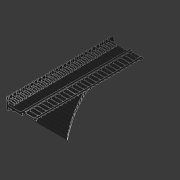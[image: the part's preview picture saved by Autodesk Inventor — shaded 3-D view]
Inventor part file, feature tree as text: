
AUTODESK INVENTOR PART (.ipt)
format: ipt  version: 2020.2 (Build 242310000, 310)  size: 4,468,224 bytes
history: native  units: in
note: dims shown in document units (in); Inventor stores cm internally (conversion verified against a paired STEP export)
features: other x35, extrude x15, loft x3, fillet x2, pattern_linear x2, sketch x1, projected_geometry x1
ambient origin geometry x8: Origin, YZ Plane, XZ Plane, XY Plane, X Axis, Y Axis, Z Axis, Center Point
bodies: Body1 (feature_tree), Body2 (feature_tree)
feature tree (59):
  other  "CrossSection1"
  other  "CrossSection2"
  other  "CrossSection3"
  other  "Whole"
  other  "Vertical Midplane"
  other  "Horizontal Midplane"
  extrude  "Block"  Depth=0.5906in
  extrude  "Hinge Protrusion"  Depth=0.5906in
  other  "Resonator Profile"
  extrude  "Resonator"  Depth=0.5906in
  extrude  "Resonator Cut"  TaperAngle=0.0deg  [1 undecoded]
  extrude  "Duct Cavity"  Depth=0.5906in
  other  "Duct Cavity Plane"
  loft  "Duct Entrance Loft"
  other  "Whistle Path Midplane"
  other  "Slit Loft To"
  loft  "Slit Loft"
  extrude  "Slit"  TaperAngle=0.0deg  [1 undecoded]
  other  "Fitting"
  extrude  "Edge Cut"  Depth=0.5906in
  other  "Edge Plane"
  other  "Edge Sketch"
  loft  "Edge Loft"
  extrude  "Edge"  Depth=0.5906in
  other  "Edge Cut Plane"
  extrude  "Spring Steel Slot"  TaperAngle=0.0deg  [1 undecoded]
  fillet  "Duct Fillet"  Radius=0.251in
  pattern_linear  "Channel Repetition"  Spacing1=0.1528in  [1 undecoded]
  extrude  "Edge Length Cut"  Depth=0.5906in
  other  "Tube Length Curve"
  extrude  "Long Tubes Length Cut"  Depth=0.5906in
  extrude  "Short Tubes Length Cut"  Depth=0.251in
  extrude  "Whistle Walls"  Depth=0.5906in
  fillet  "Whistle Wall Fillet"  Radius=0.2559in
  pattern_linear  "Whistle Wall Repetition"  Spacing1=0.8957in  [1 undecoded]
  other  "End-of-block Plane"
  extrude  "Manifold Slots"  Depth=0.5906in
  extrude  "Extension for Top C Key"  TaperAngle=0.0deg  [1 undecoded]
  other  "Split Plane"
  other  "Split for Printing"
  other  "Block Profile"
  other  "Fitting Sketch"
  other  "Duct Cavity Profile"
  other  "Duct Entrance Loft From"
  other  "Hinge Protrusion Sketch"
  other  "Edge Cut Sketch"
  other  "Edges3"
  other  "Edge Length Curve"
  other  "Whistle Wall Sketch"
  other  "2D Equation Curve10"
  other  "2D Equation Curve11"
  other  "Duct Entrance Loft To"
  other  "Slit Loft From"
  other  "Manifold Slot Sketch"
  other  "Spring Steel Slot Sketch"
  sketch  "Sketch27"  dims[d6=0.0in d7=9.8425in d9=0.4724in d20=0.3153in d21=0.0in d58=0.502in d59=0.0in d62=2.3498in d63=0.0in d70=0.1969in d80=90.0deg d105=0.2362in d106=0.0in d109=0.251in d111=0.1528in d112=0.1245in d114=0.1528in d115=0.251in d148=0.0197in d150=0.2559in d151=0.8957in d152=0.502in d154=0.0in d162=0.251in d163=0.2362in d165=0.251in d166=0.2461in d167=0.0in d171=0.2362in d174=0.502in d175=0.4429in d176=0.0in d177=90.0deg d178=0.0in d179=90.0deg d185=0.3788in d186=0.0in d189=0.1873in d190=28.3465in d191=38.2136in d198=0.0803in d199=0.0in d200=0.0197in d201=0.0787in d202=-0.125in d203=0.7874in d206=0.2559in d209=0.0in d211=9.8425in d213=0.4724in d214=0.2362in d216=0.4429in d217=0.502in d252=28.3465in d253=38.2136in d254=28.3465in d255=38.2136in d256=-0.1575in d257=0.2362in d258=0.2151in d259=0.251in d261=0.0in d262=90.0deg d263=0.0in d264=90.0deg d265=11.8406in d266=6.7754in d276=0.502in d277=0.4429in d278=0.502in d279=0.1873in d280=3.2088in d283=0.2362in d284=0.251in d285=0.4554in d286=0.5118in d287=0.0in d288=90.0deg d289=0.0in d290=90.0deg d294=1.5748in d295=0.4872in d299=0.5906in d300=0.0in d319=0.1299in d320=0.0787in d321=0.0669in d325=0.1299in d326=0.0787in d327=0.0669in d331=0.1299in d332=0.0787in d333=0.0669in d334=0.1299in d335=0.0787in d336=0.0669in d343=1.8898in d344=1.8898in d345=0.9449in d346=1.4173in d347=0.1299in d348=0.0787in d349=0.0669in d350=0.1299in d351=0.0787in d352=0.0669in d359=1.8898in d375=0.9449in d376=0.1299in d377=0.0787in d378=0.0669in d382=1.8898in d388=0.0317in d389=0.2559in d392=0.2072in d393=0.0in d396=0.2761in d397=0.0197in d398=0.0787in d399=0.0in d400=0.7874in d403=0.0618in d405=0.0197in d406=0.0787in d407=0.0in d408=0.7874in d410=0.1102in d411=0.0in d413=0.1969in d416=0.1233in d417=0.1575in d419=0.502in d432=0.1412in d434=0.1875in d441=0.0in d442=1.5748in d443=0.0295in d444=45.0deg d445=0.502in d448=0.251in d451=0.1181in d452=0.5906in d453=0.1969in d461=0.2791in d462=0.0in d463=0.1292in d464=0.4921in d466=0.406in d467=0.0787in d468=0.1969in d137=0.0197in d138=0.0344in d139=0.0197in d140=0.0344in d207=0.0344in d208=0.0197in d267=0.0197in d268=0.0344in d269=0.0197in d270=0.0344in d281=0.0197in d282=0.0344in d414=0.0344in d415=0.0197in d425=0.0197in d426=0.0344in d427=0.0197in d428=0.0344in]
  projected_geometry  "Projected Loop5"
  other  "Upper"
  other  "Lower"
note: 6 required parameter values undecoded (feature->parameter linkage not recoverable at this tier; creation-order binding heuristic only, values carry confidence <= 0.55)
